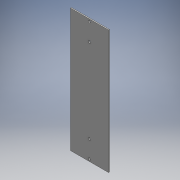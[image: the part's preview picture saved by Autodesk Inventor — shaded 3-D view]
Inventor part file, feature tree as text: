
AUTODESK INVENTOR PART (.ipt)
format: ipt  version: 2016 (Build 200138000, 138)  size: 109,568 bytes
history: native  units: mm
features: extrude x2, sketch x2, other x1
ambient origin geometry x8: Origin, YZ Plane, XZ Plane, XY Plane, X Axis, Y Axis, Z Axis, Center Point
bodies: Body1 (feature_tree)
feature tree (5):
  other  "ソリッド1"
  extrude  "押し出し1"  Depth=80.0mm
  extrude  "押し出し2"  Depth=260.0mm
  sketch  "スケッチ1"
  sketch  "スケッチ2"
